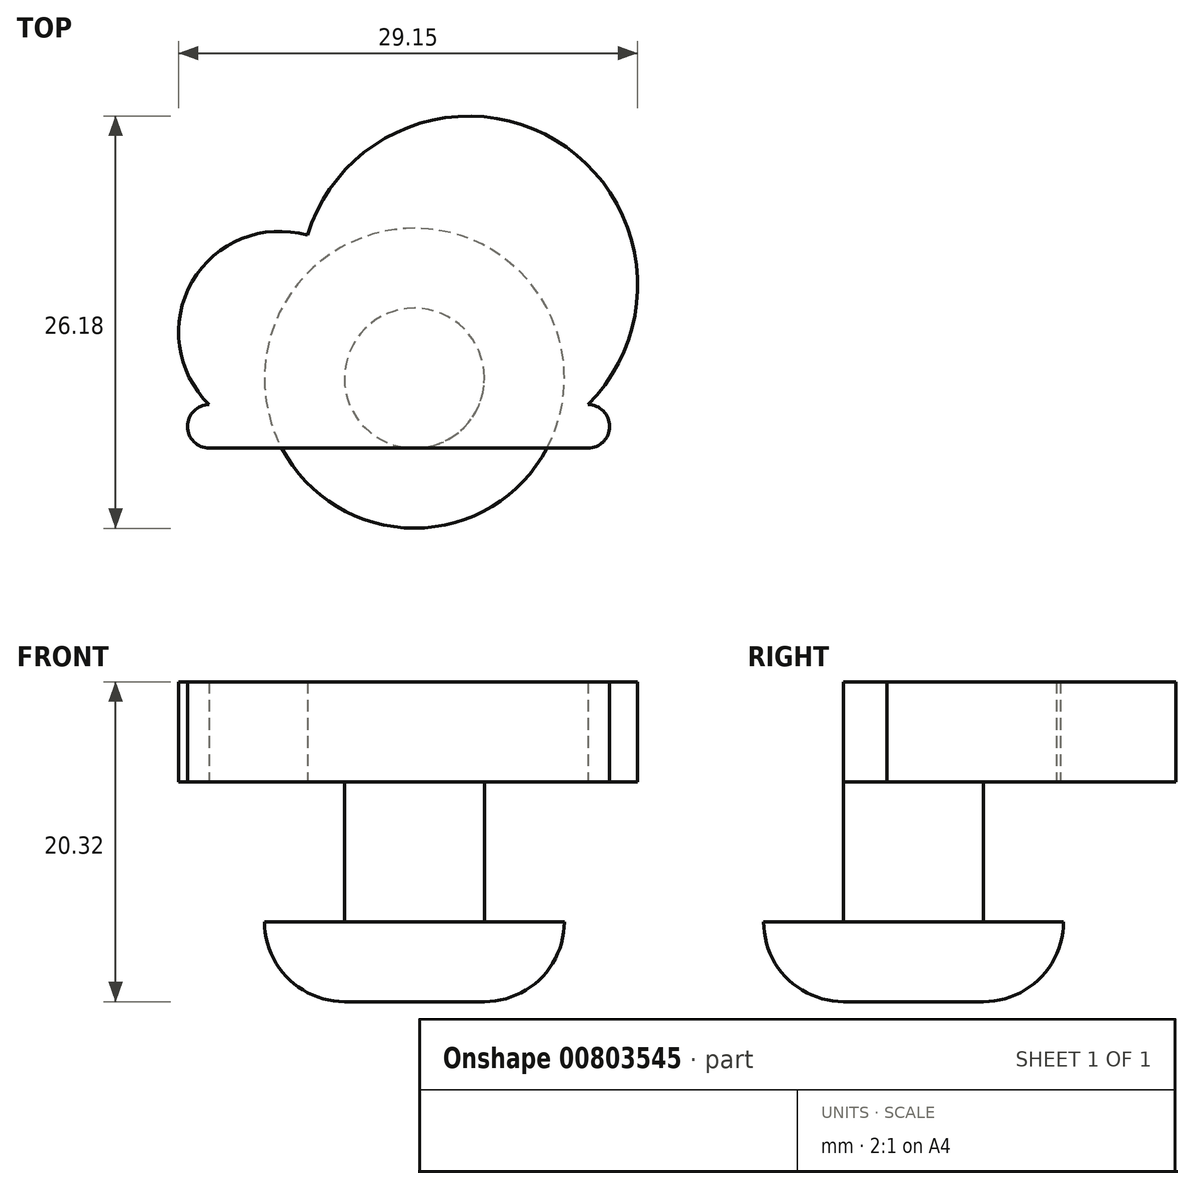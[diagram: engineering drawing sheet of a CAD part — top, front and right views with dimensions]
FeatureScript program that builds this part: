
annotation { "Feature Type Name" : "Feature", "Feature Type Description" : "" }
export const myFeature = defineFeature(function(context is Context, id is Id, definition is map)
    precondition{}
    {
        {
            var Q0;
            Q0=qCreatedBy(makeId("Top.planeOp"),FACE);
            var sketch = newSketch(context, id + "F0", { "sketchPlane" : qUnion([Q0])});
            skCircle(sketch, "E0", {"center": v(0, 0) * mm, "radius": 4.45 * mm});
            skSolve(sketch);
        }
        {
            var Q0;
            Q0 = qSketchRegion(id + "F0", true);
            extrude(context, id + "F1", {"entities" : qUnion([Q0]), "depth" : 8.9 * mm, "offsetDistance" : 25.4 * mm});
        }
        {
            var Q0;
            Q0=makeQuery(id+"F1.opExtrude","CAP_FACE",FACE,{"disambiguationData":[OSD([sQuery(id+"F0.wireOp",EDGE,"E0")])],"isStart":false});
            var sketch = newSketch(context, id + "F2", { "sketchPlane" : qUnion([Q0])});
            skLineSegment(sketch, "E1", {"start": v(11.02, -4.44) * mm, "end": v(-13.03, -4.45) * mm});
            skLineSegment(sketch, "E2", {"start": v(-13.03, -1.67) * mm, "end": v(11.02, -1.67) * mm});
            skArc(sketch, "E3", {"start": v(-13.03, -1.67) * mm, "mid": v(-14.41, -3.06) * mm, "end": v(-13.03, -4.45) * mm});
            skArc(sketch, "E4", {"start": v(11.02, -4.45) * mm, "mid": v(12.4, -3.06) * mm, "end": v(11.02, -1.67) * mm});
            skArc(sketch, "E5", {"start": v(-4.12, -1.67) * mm, "mid": v(-8.57, 9.33) * mm, "end": v(-13.03, -1.67) * mm});
            skArc(sketch, "E6", {"start": v(11.02, -1.67) * mm, "mid": v(3.45, 16.65) * mm, "end": v(-4.12, -1.67) * mm});
            skSolve(sketch);
        }
        {
            var Q0;
            Q0 = qSketchRegion(id + "F2", true);
            extrude(context, id + "F3", {"entities" : qUnion([Q0]), "operationType" : NewBodyOperationType.ADD, "depth" : 6.35 * mm, "offsetDistance" : 25.4 * mm});
        }
        {
            var Q0;
            Q0=makeQuery(id+"F1.opExtrude","CAP_FACE",FACE,{"disambiguationData":[OSD([sQuery(id+"F0.wireOp",EDGE,"E0")])],"isStart":true});
            var sketch = newSketch(context, id + "F4", { "sketchPlane" : qUnion([Q0])});
            skCircle(sketch, "E7", {"center": v(0, 0) * mm, "radius": 9.53 * mm});
            skSolve(sketch);
        }
        {
            var Q0;
            Q0 = qSketchRegion(id + "F4", true);
            extrude(context, id + "F5", {"entities" : qUnion([Q0]), "operationType" : NewBodyOperationType.ADD, "depth" : 5.08 * mm, "offsetDistance" : 25.4 * mm});
        }
        {
            var Q0;
            Q0=makeQuery(id+"F5.opExtrude","CAP_EDGE",EDGE,{"disambiguationData":[OSD([sQuery(id+"F4.wireOp",EDGE,"E7")])],"isStart":false});
            fillet(context, id + "F6", {"entities" : qUnion([Q0]), "radius" : 5.08 * mm, "tangentPropagation" : true, "allowEdgeOverflow" : false});
        }
    });
